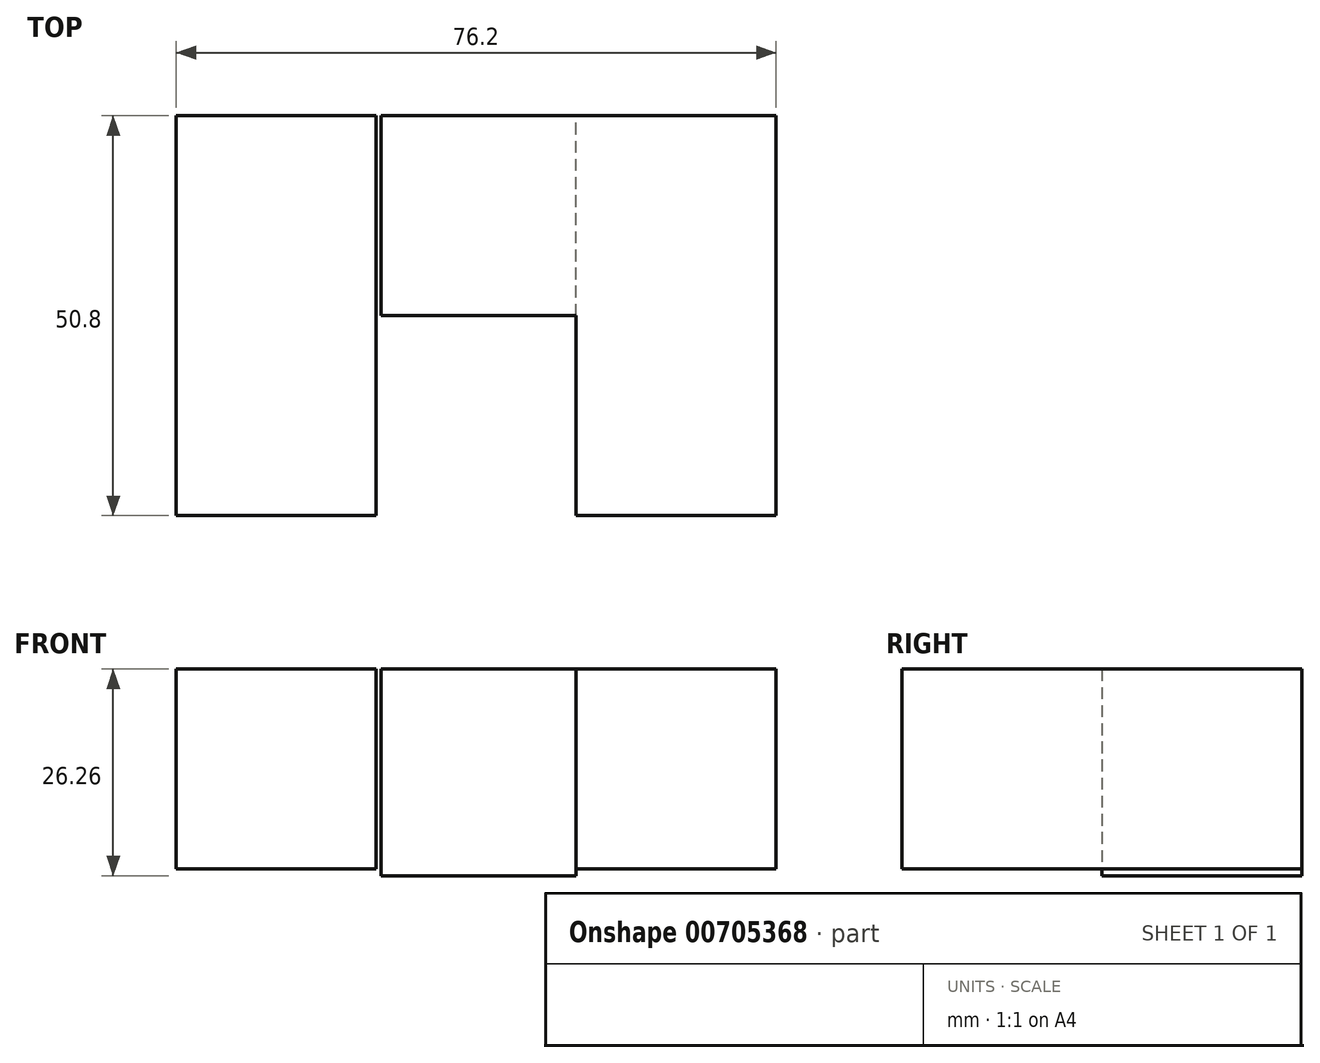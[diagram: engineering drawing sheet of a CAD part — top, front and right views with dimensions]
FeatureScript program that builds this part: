
annotation { "Feature Type Name" : "Feature", "Feature Type Description" : "" }
export const myFeature = defineFeature(function(context is Context, id is Id, definition is map)
    precondition{}
    {
        {
            var Q0;
            Q0=qCreatedBy(makeId("Front.planeOp"),FACE);
            var sketch = newSketch(context, id + "F0", { "sketchPlane" : qUnion([Q0])});
            skLineSegment(sketch, "E0.bottom", {"start": v(0, 0) * mm, "end": v(-25.4, 0) * mm});
            skLineSegment(sketch, "E0.top", {"start": v(0, 19.05) * mm, "end": v(-25.4, 19.05) * mm});
            skLineSegment(sketch, "E0.left", {"start": v(0, 0) * mm, "end": v(0, 19.05) * mm});
            skLineSegment(sketch, "E0.right", {"start": v(-25.4, 0) * mm, "end": v(-25.4, 19.05) * mm});
            skLineSegment(sketch, "E1.bottom", {"start": v(-25.4, 19.05) * mm, "end": v(0, 19.05) * mm});
            skLineSegment(sketch, "E1.top", {"start": v(-25.4, 0) * mm, "end": v(0, 0) * mm});
            skLineSegment(sketch, "E1.left", {"start": v(-25.4, 19.05) * mm, "end": v(-25.4, 0) * mm});
            skLineSegment(sketch, "E1.right", {"start": v(0, 19.05) * mm, "end": v(0, 0) * mm});
            skLineSegment(sketch, "E2.bottom", {"start": v(0, 0) * mm, "end": v(25.4, 0) * mm});
            skLineSegment(sketch, "E2.top", {"start": v(0, -25.4) * mm, "end": v(25.4, -25.4) * mm});
            skLineSegment(sketch, "E2.left", {"start": v(0, 0) * mm, "end": v(0, -25.4) * mm});
            skLineSegment(sketch, "E2.right", {"start": v(25.4, 0) * mm, "end": v(25.4, -25.4) * mm});
            skLineSegment(sketch, "E3.bottom", {"start": v(-25.4, 0) * mm, "end": v(-50.8, 0) * mm});
            skLineSegment(sketch, "E3.top", {"start": v(-25.4, -25.4) * mm, "end": v(-50.8, -25.4) * mm});
            skLineSegment(sketch, "E3.left", {"start": v(-25.4, 0) * mm, "end": v(-25.4, -25.4) * mm});
            skLineSegment(sketch, "E3.right", {"start": v(-50.8, 0) * mm, "end": v(-50.8, -25.4) * mm});
            skLineSegment(sketch, "E4.top", {"start": v(-25.4, -25.4) * mm, "end": v(0, -25.4) * mm});
            skPoint(sketch, "E5.0", {"position": v(0, 0) * mm});
            skSolve(sketch);
        }
        {
            var Q0;
            Q0=makeQuery(id+"F0.imprint","IMPRINT",FACE,{"disambiguationData":[TD([[makeQuery(id+"F0.imprint","IMPRINT",EDGE,{"derivedFrom":sQuery(id+"F0.wireOp",EDGE,"E3.bottom")}),1.0]])]});
            var Q1;
            Q1=makeQuery(id+"F0.imprint","IMPRINT",FACE,{"disambiguationData":[TD([[makeQuery(id+"F0.imprint","IMPRINT",EDGE,{"derivedFrom":sQuery(id+"F0.wireOp",EDGE,"E2.bottom")}),-1.0]])]});
            extrude(context, id + "F1", {"entities" : qUnion([Q0, Q1]), "depth" : 50.8 * mm, "offsetDistance" : 25.4 * mm});
        }
        {
            var Q0;
            Q0=qCreatedBy(makeId("Front.planeOp"),FACE);
            var sketch = newSketch(context, id + "F2", { "sketchPlane" : qUnion([Q0])});
            skLineSegment(sketch, "E6.bottom", {"start": v(0, 0) * mm, "end": v(-24.76, 0) * mm});
            skLineSegment(sketch, "E6.top", {"start": v(0, -26.26) * mm, "end": v(-24.76, -26.26) * mm});
            skLineSegment(sketch, "E6.left", {"start": v(0, 0) * mm, "end": v(0, -26.26) * mm});
            skLineSegment(sketch, "E6.right", {"start": v(-24.76, 0) * mm, "end": v(-24.76, -26.26) * mm});
            skLineSegment(sketch, "E7.bottom", {"start": v(-24.76, 0) * mm, "end": v(0, 0) * mm});
            skLineSegment(sketch, "E7.top", {"start": v(-24.76, 23) * mm, "end": v(0, 23) * mm});
            skLineSegment(sketch, "E7.left", {"start": v(-24.76, 0) * mm, "end": v(-24.76, 23) * mm});
            skLineSegment(sketch, "E7.right", {"start": v(0, 0) * mm, "end": v(0, 23) * mm});
            skSolve(sketch);
        }
        {
            var Q0;
            Q0=makeQuery(id+"F2.imprint","IMPRINT",FACE,{"disambiguationData":[TD([[makeQuery(id+"F2.imprint","IMPRINT",EDGE,{"derivedFrom":sQuery(id+"F2.wireOp",EDGE,"E6.top")}),-1.0]])]});
            var Q1;
            Q1=makeQuery(id+"F2.imprint","IMPRINT",FACE,{"disambiguationData":[TD([[makeQuery(id+"F2.imprint","IMPRINT",EDGE,{"derivedFrom":sQuery(id+"F2.wireOp",EDGE,"E7.bottom")}),1.0]])]});
            extrude(context, id + "F3", {"entities" : qUnion([Q0, Q1]), "operationType" : NewBodyOperationType.ADD, "depth" : 25.4 * mm, "offsetDistance" : 25.4 * mm});
        }
    });
